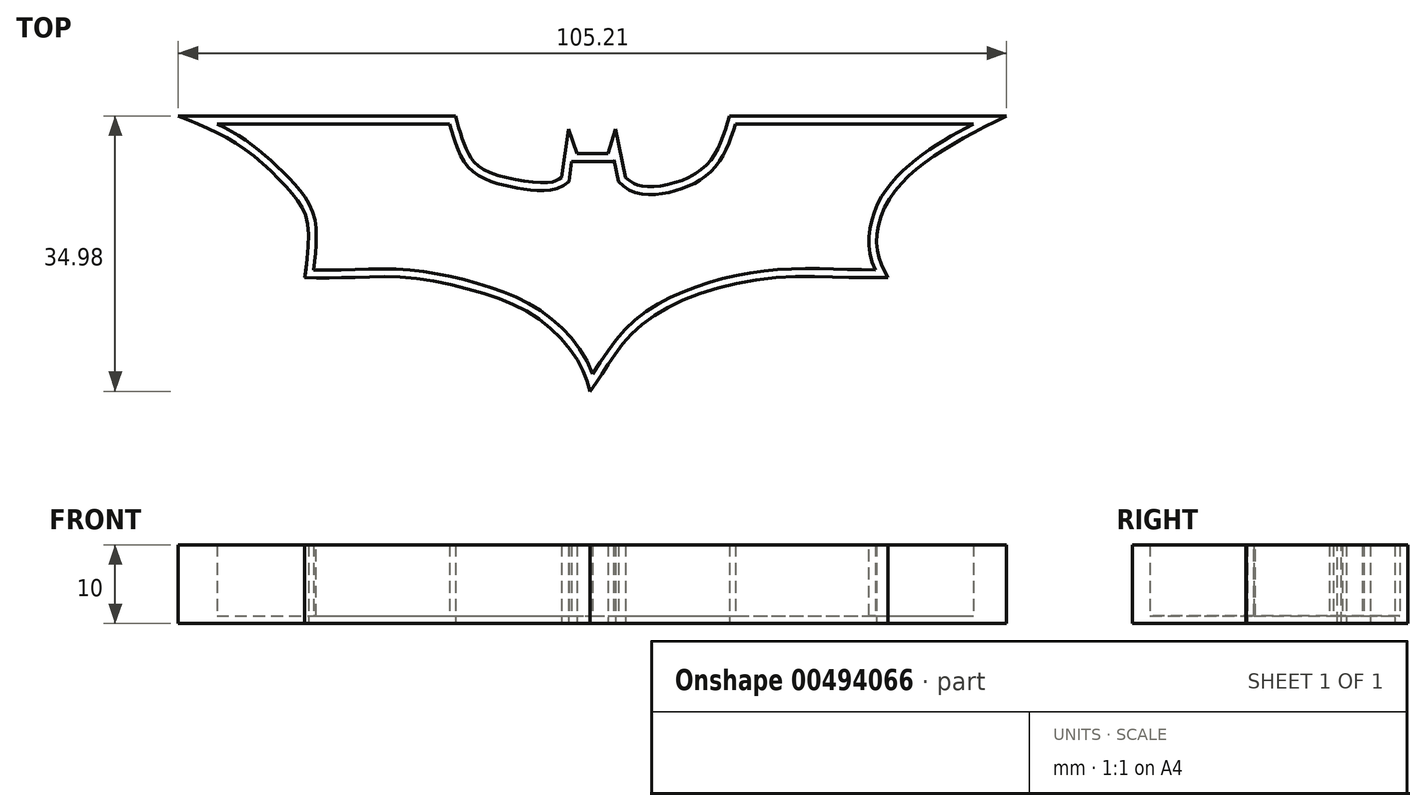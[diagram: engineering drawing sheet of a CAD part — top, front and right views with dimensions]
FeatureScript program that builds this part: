
annotation { "Feature Type Name" : "Feature", "Feature Type Description" : "" }
export const myFeature = defineFeature(function(context is Context, id is Id, definition is map)
    precondition{}
    {
        {
            var Q0;
            Q0=qCreatedBy(makeId("Top.planeOp"),FACE);
            var sketch = newSketch(context, id + "F0", { "sketchPlane" : qUnion([Q0])});
            skLineSegment(sketch, "E0", {"start": v(-52.3, 24.78) * mm, "end": v(-17.1, 24.78) * mm});
            skLineSegment(sketch, "E1", {"start": v(17.71, 24.78) * mm, "end": v(52.9, 24.78) * mm});
            skFitSpline(sketch, "E2", {"points": [v(-52.3, 24.78) * mm, v(-44.7, 21.13) * mm, v(-38.08, 15.23) * mm, v(-35.78, 9.98) * mm, v(-36.24, 4.24) * mm, v(-36.24, 4.24) * mm], "startDerivative": vector(30.19, -12.36) * mm, "endDerivative": vector(-2.54, -8.3) * mm});
            skFitSpline(sketch, "E3", {"points": [v(-36.24, 4.24) * mm, v(-30.94, 4.24) * mm, v(-23.3, 4.24) * mm, v(-13.4, 2.2) * mm, v(-6.26, -1.18) * mm, v(-1.63, -6.2) * mm, v(0, -10.2) * mm], "startDerivative": vector(34.96, -0.51) * mm, "endDerivative": vector(9.19, -29.78) * mm});
            skFitSpline(sketch, "E4", {"points": [v(0, -10.2) * mm, v(2.13, -7.07) * mm, v(5.39, -2.8) * mm, v(12.02, 1.45) * mm, v(23.67, 4.24) * mm, v(34.2, 4.24) * mm, v(37.58, 4.24) * mm, v(37.83, 4.24) * mm], "startDerivative": vector(17.1, 24.83) * mm, "endDerivative": vector(6.05, -0.06) * mm});
            skFitSpline(sketch, "E5", {"points": [v(37.83, 4.24) * mm, v(36.45, 8.09) * mm, v(37.83, 13.88) * mm, v(43.59, 19.6) * mm, v(52.9, 24.78) * mm], "startDerivative": vector(-9.61, 18.89) * mm, "endDerivative": vector(32, 15.67) * mm});
            skFitSpline(sketch, "E6", {"points": [v(-17.1, 24.78) * mm, v(-15.78, 20.74) * mm, v(-13.28, 17.86) * mm, v(-5.14, 16.35) * mm, v(-3.63, 16.98) * mm], "startDerivative": vector(4.56, -16.72) * mm, "endDerivative": vector(6.68, 5.06) * mm});
            skFitSpline(sketch, "E7", {"points": [v(-3.63, 16.98) * mm, v(-2.76, 23.12) * mm], "startDerivative": vector(0.88, 6.14) * mm, "endDerivative": vector(0.88, 6.14) * mm});
            skFitSpline(sketch, "E8", {"points": [v(-2.76, 23.12) * mm, v(-1.63, 19.99) * mm], "startDerivative": vector(1.13, -3.13) * mm, "endDerivative": vector(1.13, -3.13) * mm});
            skFitSpline(sketch, "E9", {"points": [v(-1.63, 19.99) * mm, v(-0.4, 19.99) * mm, v(2.25, 19.99) * mm], "startDerivative": vector(2.74, 0) * mm, "endDerivative": vector(4.9, 0) * mm});
            skFitSpline(sketch, "E10", {"points": [v(2.25, 19.99) * mm, v(3.26, 23.12) * mm], "startDerivative": vector(1, 3.13) * mm, "endDerivative": vector(1, 3.13) * mm});
            skFitSpline(sketch, "E11", {"points": [v(3.26, 23.12) * mm, v(4.5, 16.98) * mm], "startDerivative": vector(1.25, -6.14) * mm, "endDerivative": vector(1.25, -6.14) * mm});
            skFitSpline(sketch, "E12", {"points": [v(4.5, 16.98) * mm, v(6.64, 15.85) * mm, v(14.15, 17.98) * mm, v(17.71, 24.78) * mm], "startDerivative": vector(7.46, -6.64) * mm, "endDerivative": vector(5.86, 19.69) * mm});
            skSolve(sketch);
        }
        {
            var Q0;
            Q0=makeQuery(id+"F0.imprint","IMPRINT",FACE,{"disambiguationData":[TD([[makeQuery(id+"F0.imprint","IMPRINT",EDGE,{"derivedFrom":sQuery(id+"F0.wireOp",EDGE,"E0")}),-1.0]])]});
            extrude(context, id + "F1", {"entities" : qUnion([Q0]), "depth" : 10 * mm});
        }
        {
            var Q0;
            Q0=makeQuery(id+"F1.opExtrude","CAP_FACE",FACE,{"disambiguationData":[OSD([sQuery(id+"F0.wireOp",EDGE,"E0"),sQuery(id+"F0.wireOp",EDGE,"E1"),sQuery(id+"F0.wireOp",EDGE,"E2"),sQuery(id+"F0.wireOp",EDGE,"E3"),sQuery(id+"F0.wireOp",EDGE,"E4"),sQuery(id+"F0.wireOp",EDGE,"E5"),sQuery(id+"F0.wireOp",EDGE,"E6"),sQuery(id+"F0.wireOp",EDGE,"E7"),sQuery(id+"F0.wireOp",EDGE,"E8"),sQuery(id+"F0.wireOp",EDGE,"E9"),sQuery(id+"F0.wireOp",EDGE,"E10"),sQuery(id+"F0.wireOp",EDGE,"E11"),sQuery(id+"F0.wireOp",EDGE,"E12")])],"isStart":false});
            shell(context, id + "F2", {"entities" : qUnion([Q0]), "thickness" : 1 * mm});
        }
    });
